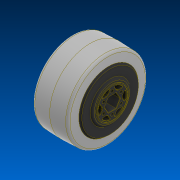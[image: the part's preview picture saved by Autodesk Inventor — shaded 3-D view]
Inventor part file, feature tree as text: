
AUTODESK INVENTOR PART (.ipt)
format: ipt  version: 2022.2 (Build 262287000, 287)  size: 1,509,376 bytes
history: native  units: in
note: dims shown in document units (in); Inventor stores cm internally (conversion verified against a paired STEP export)
features: revolve x1
ambient origin geometry x8: Origin, YZ Plane, XZ Plane, XY Plane, X Axis, Y Axis, Z Axis, Center Point
bodies: Solid1 (feature_tree)
feature tree (1):
  revolve  "Revolve1"  [1 undecoded]
note: 1 required parameter value undecoded (feature->parameter linkage not recoverable at this tier; creation-order binding heuristic only, values carry confidence <= 0.55)
